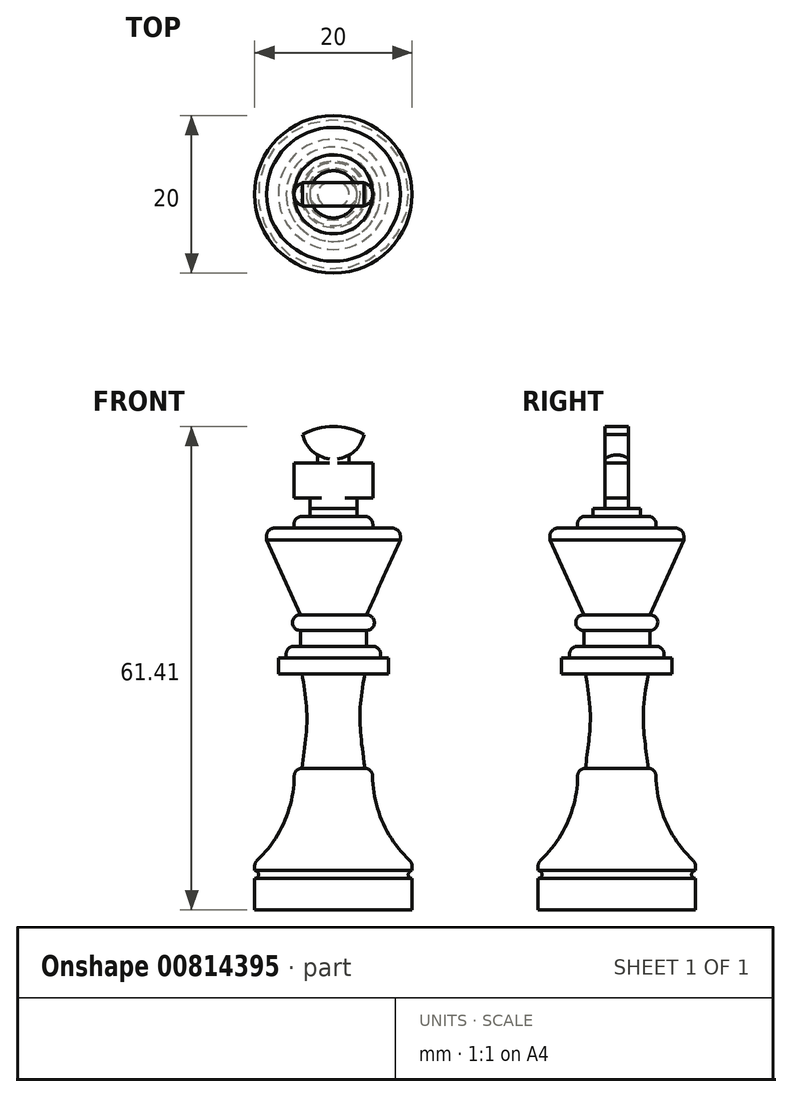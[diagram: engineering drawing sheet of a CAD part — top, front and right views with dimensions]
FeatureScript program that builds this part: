
annotation { "Feature Type Name" : "Feature", "Feature Type Description" : "" }
export const myFeature = defineFeature(function(context is Context, id is Id, definition is map)
    precondition{}
    {
        {
            var Q0;
            Q0=qCreatedBy(makeId("Front.planeOp"),FACE);
            var sketch = newSketch(context, id + "F0", { "sketchPlane" : qUnion([Q0])});
            skLineSegment(sketch, "E0.top", {"start": v(-10, 0) * mm, "end": v(10, 0) * mm, "construction": true});
            skLineSegment(sketch, "E0.left", {"start": v(10, 57) * mm, "end": v(10, 0) * mm, "construction": true});
            skLineSegment(sketch, "E0.right", {"start": v(-10, 57) * mm, "end": v(-10, 0) * mm, "construction": true});
            skLineSegment(sketch, "E1", {"start": v(0, 0) * mm, "end": v(0, 4) * mm, "construction": true});
            skLineSegment(sketch, "E2", {"start": v(0, 4) * mm, "end": v(-10, 4) * mm, "construction": true});
            skLineSegment(sketch, "E3", {"start": v(0, 4) * mm, "end": v(0, 5) * mm, "construction": true});
            skLineSegment(sketch, "E4", {"start": v(0, 5) * mm, "end": v(-10, 5) * mm, "construction": true});
            skLineSegment(sketch, "E5", {"start": v(0, 5) * mm, "end": v(0, 6) * mm, "construction": true});
            skLineSegment(sketch, "E6", {"start": v(0, 6) * mm, "end": v(-10, 6) * mm, "construction": true});
            skLineSegment(sketch, "E7", {"start": v(-9, 5) * mm, "end": v(-9, 4) * mm, "construction": true});
            skLineSegment(sketch, "E8", {"start": v(0, 6) * mm, "end": v(0, 18) * mm, "construction": true});
            skLineSegment(sketch, "E9", {"start": v(0, 18) * mm, "end": v(0, 30) * mm, "construction": true});
            skLineSegment(sketch, "E10", {"start": v(0, 0) * mm, "end": v(-10, 0) * mm});
            skLineSegment(sketch, "E11", {"start": v(-10, 4) * mm, "end": v(-10, 0) * mm});
            skArc(sketch, "E12", {"start": v(-10, 4) * mm, "mid": v(-9.5, 4.5) * mm, "end": v(-10, 5) * mm});
            skLineSegment(sketch, "E13", {"start": v(-10, 5) * mm, "end": v(-10, 6) * mm});
            skLineSegment(sketch, "E14", {"start": v(0, 18) * mm, "end": v(-10, 18) * mm, "construction": true});
            skLineSegment(sketch, "E15", {"start": v(0, 30) * mm, "end": v(-10, 30) * mm, "construction": true});
            skArc(sketch, "E16", {"start": v(-10, 6) * mm, "mid": v(-6.13, 11.43) * mm, "end": v(-5, 18) * mm});
            skLineSegment(sketch, "E17", {"start": v(-5, 18) * mm, "end": v(-4, 18) * mm});
            skLineSegment(sketch, "E18", {"start": v(0.27, 32) * mm, "end": v(-10, 32) * mm, "construction": true});
            skFitSpline(sketch, "E19", {"points": [v(-4, 18) * mm, v(-4, 30) * mm], "startDerivative": vector(2.23, 16.47) * mm, "endDerivative": vector(-2.8, 14.94) * mm});
            skLineSegment(sketch, "E20", {"start": v(-4, 30) * mm, "end": v(-7, 30) * mm});
            skLineSegment(sketch, "E21", {"start": v(-7, 30) * mm, "end": v(-7, 32) * mm});
            skLineSegment(sketch, "E22", {"start": v(-7, 32) * mm, "end": v(-6, 32) * mm});
            skLineSegment(sketch, "E23", {"start": v(0, 33.5) * mm, "end": v(-10, 33.5) * mm, "construction": true});
            skLineSegment(sketch, "E24", {"start": v(0, 35.5) * mm, "end": v(-10, 35.5) * mm, "construction": true});
            skLineSegment(sketch, "E25", {"start": v(0, 37.5) * mm, "end": v(-10, 37.5) * mm, "construction": true});
            skLineSegment(sketch, "E26", {"start": v(-6, 32) * mm, "end": v(-6, 33.5) * mm});
            skLineSegment(sketch, "E27", {"start": v(-6, 33.5) * mm, "end": v(-4.2, 33.5) * mm});
            skLineSegment(sketch, "E28", {"start": v(-4.2, 33.5) * mm, "end": v(-4.2, 35.5) * mm});
            skArc(sketch, "E29", {"start": v(-4.2, 37.5) * mm, "mid": v(-5.2, 36.5) * mm, "end": v(-4.2, 35.5) * mm});
            skLineSegment(sketch, "E30", {"start": v(-10, 47) * mm, "end": v(0, 47) * mm, "construction": true});
            skLineSegment(sketch, "E31", {"start": v(-10, 48.5) * mm, "end": v(0, 48.5) * mm, "construction": true});
            skLineSegment(sketch, "E32", {"start": v(-8.5, 48.5) * mm, "end": v(-8.5, 47) * mm});
            skLineSegment(sketch, "E33", {"start": v(0, 50) * mm, "end": v(-10, 50) * mm, "construction": true});
            skLineSegment(sketch, "E34", {"start": v(-10, 51) * mm, "end": v(0, 51) * mm, "construction": true});
            skLineSegment(sketch, "E35", {"start": v(-3, 50) * mm, "end": v(-3, 51) * mm});
            skLineSegment(sketch, "E36", {"start": v(-10, 52) * mm, "end": v(0, 52) * mm, "construction": true});
            skLineSegment(sketch, "E37", {"start": v(-8.5, 47) * mm, "end": v(-4.2, 37.5) * mm});
            skLineSegment(sketch, "E38", {"start": v(-8.5, 48.5) * mm, "end": v(-5, 48.5) * mm});
            skLineSegment(sketch, "E39", {"start": v(-5, 48.5) * mm, "end": v(-5, 50) * mm});
            skLineSegment(sketch, "E40", {"start": v(-5, 50) * mm, "end": v(-3, 50) * mm});
            skLineSegment(sketch, "E41", {"start": v(-3, 51) * mm, "end": v(0, 51) * mm});
            skLineSegment(sketch, "E42", {"start": v(0, 51) * mm, "end": v(0, 0) * mm});
            skSolve(sketch);
        }
        {
            var Q0;
            Q0=qSketchRegion(id+"F0",true);
            var Q1;
            Q1=sQuery(id+"F0.wireOp",EDGE,"E42");
            revolve(context, id + "F1", {"surfaceOperationType" : NewSurfaceOperationType.NEW, "entities" : qUnion([Q0]), "axis" : qUnion([Q1]), "revolveType" : RevolveType.FULL});
        }
        {
            var Q0;
            Q0=makeQuery(id+"F1.opRevolve","SWEPT_EDGE",EDGE,{"disambiguationData":[OSD([sQuery(id+"F0.wireOp",EDGE,"E13"),sQuery(id+"F0.wireOp",EDGE,"E16")])]});
            var Q1;
            Q1=makeQuery(id+"F1.opRevolve","SWEPT_EDGE",EDGE,{"disambiguationData":[OSD([sQuery(id+"F0.wireOp",EDGE,"E16"),sQuery(id+"F0.wireOp",EDGE,"E17")])]});
            var Q2;
            Q2=makeQuery(id+"F1.opRevolve","SWEPT_EDGE",EDGE,{"disambiguationData":[OSD([sQuery(id+"F0.wireOp",EDGE,"E26"),sQuery(id+"F0.wireOp",EDGE,"E27")])]});
            var Q3;
            Q3=makeQuery(id+"F1.opRevolve","SWEPT_EDGE",EDGE,{"disambiguationData":[OSD([sQuery(id+"F0.wireOp",EDGE,"E32"),sQuery(id+"F0.wireOp",EDGE,"E38")])]});
            var Q4;
            Q4=makeQuery(id+"F1.opRevolve","SWEPT_EDGE",EDGE,{"disambiguationData":[OSD([sQuery(id+"F0.wireOp",EDGE,"E39"),sQuery(id+"F0.wireOp",EDGE,"E40")])]});
            fillet(context, id + "F2", {"entities" : qUnion([Q0, Q1, Q2, Q3, Q4]), "radius" : 1 * mm, "tangentPropagation" : true, "allowEdgeOverflow" : false});
        }
        {
            var Q0;
            Q0=qCreatedBy(makeId("Front.planeOp"),FACE);
            var sketch = newSketch(context, id + "F3", { "sketchPlane" : qUnion([Q0])});
            skLineSegment(sketch, "E43", {"start": v(0, 51) * mm, "end": v(-3, 51) * mm});
            skLineSegment(sketch, "E44", {"start": v(-3, 51) * mm, "end": v(-3, 52.3) * mm});
            skLineSegment(sketch, "E45", {"start": v(-3, 52.3) * mm, "end": v(-5, 52.3) * mm});
            skLineSegment(sketch, "E46", {"start": v(-5, 52.3) * mm, "end": v(-5, 56.8) * mm});
            skLineSegment(sketch, "E47", {"start": v(5, 56.8) * mm, "end": v(5, 52.3) * mm});
            skLineSegment(sketch, "E48", {"start": v(5, 52.3) * mm, "end": v(3, 52.3) * mm});
            skLineSegment(sketch, "E49", {"start": v(3, 52.3) * mm, "end": v(3, 51) * mm});
            skLineSegment(sketch, "E50", {"start": v(3, 51) * mm, "end": v(0, 51) * mm});
            skLineSegment(sketch, "E51", {"start": v(-5, 56.8) * mm, "end": v(-2, 56.8) * mm});
            skLineSegment(sketch, "E52", {"start": v(-2, 56.8) * mm, "end": v(-2, 57.8) * mm});
            skArc(sketch, "E53", {"start": v(-3.9, 60.4) * mm, "mid": v(-3.22, 58.9) * mm, "end": v(-2, 57.8) * mm});
            skLineSegment(sketch, "E54", {"start": v(5, 56.8) * mm, "end": v(2, 56.8) * mm});
            skLineSegment(sketch, "E55", {"start": v(2, 56.8) * mm, "end": v(2, 57.8) * mm});
            skLineSegment(sketch, "E56", {"start": v(0, 51) * mm, "end": v(0, 61.4) * mm, "construction": true});
            skArc(sketch, "E57", {"start": v(2, 57.8) * mm, "mid": v(3.22, 58.9) * mm, "end": v(3.9, 60.4) * mm});
            skArc(sketch, "E58", {"start": v(3.9, 60.4) * mm, "mid": v(0, 61.4) * mm, "end": v(-3.9, 60.4) * mm});
            skSolve(sketch);
        }
        {
            var Q0;
            Q0=qSketchRegion(id+"F3",true);
            extrude(context, id + "F4", {"entities" : qUnion([Q0]), "operationType" : NewBodyOperationType.ADD, "endBound" : BoundingType.SYMMETRIC, "depth" : 3 * mm, "offsetDistance" : 25 * mm});
        }
        {
            var Q0;
            Q0=makeQuery(id+"F4.opExtrude","CAP_EDGE",EDGE,{"disambiguationData":[OSD([sQuery(id+"F3.wireOp",EDGE,"E46")])],"isStart":false});
            var Q1;
            Q1=makeQuery(id+"F4.opExtrude","CAP_EDGE",EDGE,{"disambiguationData":[OSD([sQuery(id+"F3.wireOp",EDGE,"E46")])],"isStart":true});
            var Q2;
            Q2=makeQuery(id+"F4.opExtrude","CAP_EDGE",EDGE,{"disambiguationData":[OSD([sQuery(id+"F3.wireOp",EDGE,"E47")])],"isStart":false});
            var Q3;
            Q3=makeQuery(id+"F4.opExtrude","CAP_EDGE",EDGE,{"disambiguationData":[OSD([sQuery(id+"F3.wireOp",EDGE,"E47")])],"isStart":true});
            var Q4;
            Q4=makeQuery(id+"F4.opExtrude","CAP_EDGE",EDGE,{"disambiguationData":[OSD([sQuery(id+"F3.wireOp",EDGE,"E52")])],"isStart":false});
            var Q5;
            Q5=makeQuery(id+"F4.opExtrude","CAP_EDGE",EDGE,{"disambiguationData":[OSD([sQuery(id+"F3.wireOp",EDGE,"E55")])],"isStart":false});
            var Q6;
            Q6=makeQuery(id+"F4.opExtrude","CAP_EDGE",EDGE,{"disambiguationData":[OSD([sQuery(id+"F3.wireOp",EDGE,"E52")])],"isStart":true});
            var Q7;
            Q7=makeQuery(id+"F4.opExtrude","CAP_EDGE",EDGE,{"disambiguationData":[OSD([sQuery(id+"F3.wireOp",EDGE,"E55")])],"isStart":true});
            var Q8;
            Q8=makeQuery(id+"F4.opExtrude","CAP_EDGE",EDGE,{"disambiguationData":[OSD([sQuery(id+"F3.wireOp",EDGE,"E49")])],"isStart":true});
            var Q9;
            Q9=makeQuery(id+"F4.opExtrude","CAP_EDGE",EDGE,{"disambiguationData":[OSD([sQuery(id+"F3.wireOp",EDGE,"E49")])],"isStart":false});
            var Q10;
            Q10=makeQuery(id+"F4.opExtrude","CAP_EDGE",EDGE,{"disambiguationData":[OSD([sQuery(id+"F3.wireOp",EDGE,"E44")])],"isStart":false});
            var Q11;
            Q11=makeQuery(id+"F4.opExtrude","CAP_EDGE",EDGE,{"disambiguationData":[OSD([sQuery(id+"F3.wireOp",EDGE,"E44")])],"isStart":true});
            fillet(context, id + "F5", {"entities" : qUnion([Q0, Q1, Q2, Q3, Q4, Q5, Q6, Q7, Q8, Q9, Q10, Q11]), "radius" : 1.5 * mm, "tangentPropagation" : true, "allowEdgeOverflow" : false});
        }
    });
